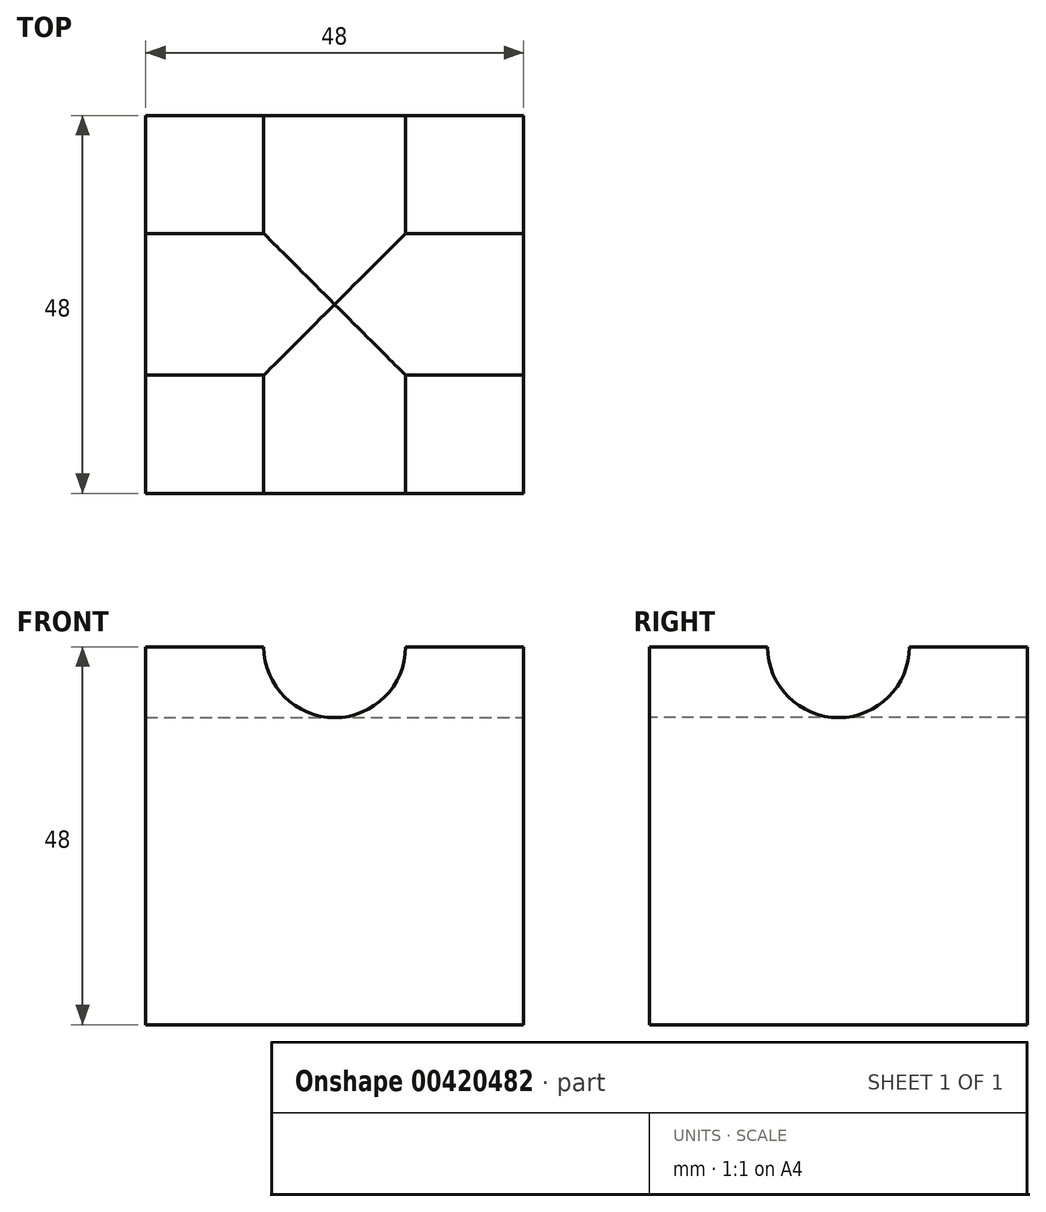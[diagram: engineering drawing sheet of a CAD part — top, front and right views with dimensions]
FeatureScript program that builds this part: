
annotation { "Feature Type Name" : "Feature", "Feature Type Description" : "" }
export const myFeature = defineFeature(function(context is Context, id is Id, definition is map)
    precondition{}
    {
        {
            var Q0;
            Q0=qCreatedBy(makeId("Front.planeOp"),FACE);
            var sketch = newSketch(context, id + "F0", { "sketchPlane" : qUnion([Q0])});
            skLineSegment(sketch, "E0.bottom", {"start": v(-24, 24) * mm, "end": v(24, 24) * mm});
            skLineSegment(sketch, "E0.top", {"start": v(-24, -24) * mm, "end": v(24, -24) * mm});
            skLineSegment(sketch, "E0.left", {"start": v(-24, 24) * mm, "end": v(-24, -24) * mm});
            skLineSegment(sketch, "E0.right", {"start": v(24, 24) * mm, "end": v(24, -24) * mm});
            skPoint(sketch, "E0.middle", {"position": v(0, 0) * mm});
            skSolve(sketch);
        }
        {
            var Q0;
            Q0=makeQuery(id+"F0.imprint","IMPRINT",FACE,{"disambiguationData":[TD([[makeQuery(id+"F0.imprint","IMPRINT",EDGE,{"derivedFrom":sQuery(id+"F0.wireOp",EDGE,"E0.bottom")}),-1.0]])]});
            extrude(context, id + "F1", {"entities" : qUnion([Q0]), "depth" : 48 * mm, "symmetric" : true});
        }
        {
            var Q0;
            Q0=makeQuery(id+"F1.opExtrude","CAP_FACE",FACE,{"disambiguationData":[OSD([sQuery(id+"F0.wireOp",EDGE,"E0.bottom"),sQuery(id+"F0.wireOp",EDGE,"E0.top"),sQuery(id+"F0.wireOp",EDGE,"E0.left"),sQuery(id+"F0.wireOp",EDGE,"E0.right")])],"isStart":false});
            var sketch = newSketch(context, id + "F2", { "sketchPlane" : qUnion([Q0])});
            skCircle(sketch, "E1", {"center": v(0, 24) * mm, "radius": 9 * mm});
            skSolve(sketch);
        }
        {
            var Q0;
            Q0 = qSketchRegion(id + "F2", true);
            extrude(context, id + "F3", {"entities" : qUnion([Q0]), "operationType" : NewBodyOperationType.REMOVE, "oppositeDirection" : true, "depth" : 48 * mm});
        }
        {
            var Q0;
            Q0=makeQuery(id+"F1.opExtrude","SWEPT_FACE",FACE,{"disambiguationData":[OSD([sQuery(id+"F0.wireOp",EDGE,"E0.right")])]});
            var sketch = newSketch(context, id + "F4", { "sketchPlane" : qUnion([Q0])});
            skCircle(sketch, "E2", {"center": v(0, 24) * mm, "radius": 9 * mm});
            skSolve(sketch);
        }
        {
            var Q0;
            {var subQ0=sQuery(id+"F4.wireOp",EDGE,"E2");var subQ1=makeQuery(id+"F1.opExtrude","SWEPT_EDGE",EDGE,{"disambiguationData":[OSD([sQuery(id+"F0.wireOp",EDGE,"E0.bottom"),sQuery(id+"F0.wireOp",EDGE,"E0.right")])]});var subQ2=makeQuery(id+"F4.imprint","INTERSECT",VERTEX,{"disambiguationData":[OD(0.0)],"derivedFrom":[subQ1,subQ0]});Q0=makeQuery(id+"F4.imprint","IMPRINT",FACE,{"disambiguationData":[TD([[makeQuery(id+"F4.imprint","IMPRINT",EDGE,{"disambiguationData":[TD([[subQ2,1.0]])],"derivedFrom":subQ0}),1.0]])]});}
            extrude(context, id + "F5", {"entities" : qUnion([Q0]), "operationType" : NewBodyOperationType.REMOVE, "oppositeDirection" : true, "depth" : 48 * mm});
        }
    });
